# Revit family: Furniture_Chairs-Stools-Benches_Svedholm_Dix-Stool
name_source: partatom
category: Furniture
revit_build: Autodesk Revit 2018 (Build: 20190510_1515(x64)
units: mm (PartAtom-declared; Revit-internal decimal feet)

## family parameters
Always vertical = No
Cut with Voids When Loaded = No
OmniClass Number = 23.21.23.00
OmniClass Title = Residential Furniture and Equipment
Room Calculation Point = No
Shared = No
Work Plane-Based = Yes

## types (1)
- ART - (203.600.005)
    BIMobject category = Chairs, Stools & Benches
    Default Elevation = 1219.2 mm  [stored 4 ft]
    Description = A stool with seat in tanned leather. Base of powder coated wire.
    Design country = Sweden
    Edition number = 1
    IFC Classification = Furniture
    Manufacturer = Svedholm
    Manufacturer country = Sweden
    Manufacturer name = Svedholm
    Material main = Leather
    Material secondary = Powder coated steel
    Model = Dix stool
    OmniClass Code = 23-21 23 00
    OmniClass Description = Residential Furniture and Equipment
    Product Guid = b98f2043-41b8-47d3-a7ef-b871f57aeeaf
    Product SKU = Dix-stool
    Product data url = https://bimobject.com
    Product family = Dix
    Product group = Stool
    Product name = Dix Stool
    Product url = https://www.svedholm.se
    QR code = https://bimobject.com
    Seat material = Svedholm - Textile - Leather
    UNSPSC Code = 56
    URL = https://www.svedholm.se
    Uniclass 1.4 Code = L8221
    Uniclass 1.4 Description = Tables

note: [stored X ft] marks values corroborated as IEEE doubles in the binary element streams (Revit-internal decimal feet)

## geometry (parser evidence)
native form markers: Sweep x2
no freeform markers — native parametric forms only
